# Revit family: Hitachi_RAC-EYHA_Outdoor_Unit_0718
name_source: partatom
category: Mechanical Equipment
revit_build: Autodesk Revit 2015 (Build: 20140223_1515(x64)
units: mm (PartAtom-declared; Revit-internal decimal feet)

## types (4) — shared parameters
Back Clearance = 100 mm  [stored 0.328084 ft]
Clearance = Default
Front Clearance = 700 mm  [stored 2.29659 ft]
Interconnecting Wires = 3 + E, 1.5 mm
Left Clearance = 100 mm  [stored 0.328084 ft]
Manufacturer = Temperzone / Hitachi
Material = Hitachi - Outdoor Unit
Outdoor Operating Temp. (cooling) C db = 46 to -15 C
Outdoor Operating Temp. (heating) C db = 24 to -15 C
Pipe Connection Size - Liquid = 6.35 mm
Pipe Height (max.) = 20m
Pipe Length (min./max.) = 3m to 30m
Power Suppy = 240 / 1
Radius pipe Top LIQUID = 3 mm  [stored 0.00984252 ft]
Recommended External Protection = 20 A
Refrigerant Pipe Charge Length = 30m
Refrigerant Type = R32
Right Clearance = 200 mm  [stored 0.656168 ft]
Top Clearance = 200 mm  [stored 0.656168 ft]
URL = www.temperzone.biz
Unit Depth = 298 mm  [stored 0.97769 ft]
Unit Width = 850 mm  [stored 2.78871 ft]

## per-type parameters (varying)
| type | Airflow - Hi | COP Heating | Cooling Capacity | Cooling Range | Description | EER Cooling | Heating Capacity | Heating Range | Height Refig Pipe (Top LIQUID) | Height Refrig Pipe (Bottom - GAS) | Model - Indoor | Pipe Connection Size - Gas | Radius Pipe Bottom GAS | Refrig Pipe Offset from Back | Sound Pressure Level (dbA) - Cool / Heat | Unit Height | Weight (kg) |
| RAC-E50YHA | 221.0 L/s | 4.06 | 5000 W | 1.2 - 5.8 kW | Hitachi Outdoor Unit RAC-E50YHA | 3.52 | 6000 W | 1.2 - 6.8 kW | 170 mm | 96 mm  [stored 0.314961 ft] | RAS-E50YHA | 12.7 mm | 6 mm  [stored 0.019685 ft] | 201 mm  [stored 0.659449 ft] | 50 / 53 | 750 mm  [stored 2.46063 ft] | 50 |
| RAC-E60YHA | 221.0 L/s | 3.82 | 6000 W | 1.2 - 7.5 kW | Hitachi Outdoor Unit RAC-E60YHA | 3.41 | 7000 W | 1.2 - 8.0 kW | 160 mm | 108 mm | RAS-E60YHA | 12.7 mm | 6 mm  [stored 0.019685 ft] | 191 mm  [stored 0.62664 ft] | 50 / 53 | 750 mm  [stored 2.46063 ft] | 50 |
| RAC-E70YHA | 300.0 L/s | 4.05 | 7000 W | 1.5 - 8.0 kW | Hitachi Outdoor Unit RAC-E70YHA | 3.48 | 8000 W | 1.5 - 8.5 kW | 170 mm | 96 mm  [stored 0.314961 ft] | RAS-E70YHA | 15.9 mm | 8 mm  [stored 0.0262467 ft] | 201 mm  [stored 0.659449 ft] | 51 / 53 | 800 mm  [stored 2.62467 ft] | 52 |
| RAC-E80YHA | 300.0 L/s | 3.8 | 8000 W | 1.5 - 8.5 kW | Hitachi Outdoor Unit RAC-E80YHA | 3.33 | 9000 W | 1.5 - 9.5 kW | 170 mm | 96 mm  [stored 0.314961 ft] | RAS-E80YHA | 15.9 mm | 8 mm  [stored 0.0262467 ft] | 201 mm  [stored 0.659449 ft] | 52 / 54 | 800 mm  [stored 2.62467 ft] | 52 |

note: column(s) folded — value = type name in every type: Model

note: [stored X ft] marks values corroborated as IEEE doubles in the binary element streams (Revit-internal decimal feet)

## geometry (parser evidence)
native form markers: Blend x4, Sweep x2
no freeform markers — native parametric forms only
